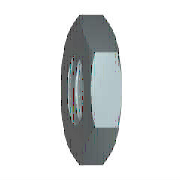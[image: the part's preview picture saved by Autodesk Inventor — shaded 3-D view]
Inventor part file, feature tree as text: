
AUTODESK INVENTOR PART (.ipt)
format: ipt  version: 2023.2 (Build 272271030, 271C)  size: 164,352 bytes
history: native  units: mm (DEFAULTED — no unit token found)
features: sketch x3, chamfer x1, hole x1, other x1, plane x1
ambient origin geometry x7: Origin, YZ Plane, XZ Plane, X Axis, Y Axis, Z Axis, Center Point
bodies: Solid1 (feature_tree), Body (feature_tree)
feature tree (7):
  chamfer  "Chamfer1"  Angle=30.0deg  [1 undecoded]
  hole  "Thread"  [1 undecoded]
  other  "Work Axis1"
  plane  "Work Plane1"
  sketch  "Sketch1"  dims[d0=9.237604mm]
  sketch  "Sketch2"  dims[d1=2.7mm]
  sketch  "Sketch3"  dims[d2=0.0mm d3=30.0deg d4=30.0deg d5=6.9mm d6=6.9mm d7=90.0deg d25=4.134mm d26=6.0mm d27=4.0mm d28=2.0mm d29=14.3117mm d30=8.0mm d31=20.594885mm d8=0.433013mm d9=30.0deg d10=0.433013mm d11=30.0deg d13=0.0mm d14=0.0mm d39=0.0mm d40=0.433013mm d41=0.433013mm d42=0.0mm]
note: 2 required parameter values undecoded (feature->parameter linkage not recoverable at this tier; creation-order binding heuristic only, values carry confidence <= 0.55)
